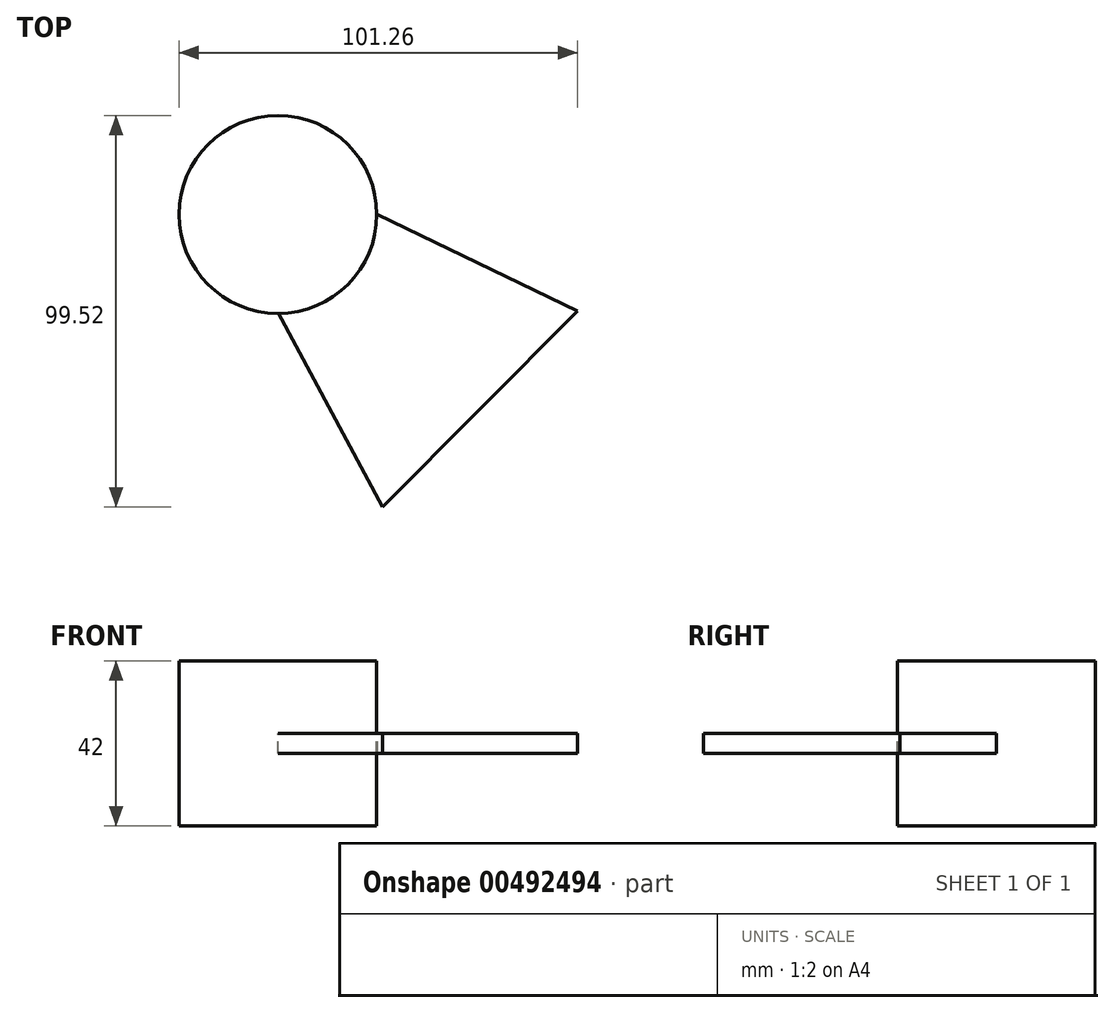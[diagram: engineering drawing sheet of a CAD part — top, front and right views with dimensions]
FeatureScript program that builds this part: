
annotation { "Feature Type Name" : "Feature", "Feature Type Description" : "" }
export const myFeature = defineFeature(function(context is Context, id is Id, definition is map)
    precondition{}
    {
        {
            var Q0;
            Q0=qCreatedBy(makeId("Top.planeOp"),FACE);
            var sketch = newSketch(context, id + "F0", { "sketchPlane" : qUnion([Q0])});
            skCircle(sketch, "E0", {"center": v(0, 0) * mm, "radius": 25.13 * mm});
            skSolve(sketch);
        }
        {
            var Q0;
            Q0=sQuery(id+"F0.wireOp",EDGE,"E0");
            extrude(context, id + "F1", {"bodyType" : ToolBodyType.SURFACE, "surfaceEntities" : qUnion([Q0]), "endBound" : BoundingType.SYMMETRIC, "depth" : 42 * mm});
        }
        {
            var Q0;
            Q0=qCreatedBy(makeId("Top.planeOp"),FACE);
            var sketch = newSketch(context, id + "F2", { "sketchPlane" : qUnion([Q0])});
            skLineSegment(sketch, "E1", {"start": v(25.35, 0) * mm, "end": v(76.13, -24.53) * mm});
            skLineSegment(sketch, "E2", {"start": v(76.13, -24.53) * mm, "end": v(26.56, -74.39) * mm});
            skLineSegment(sketch, "E3", {"start": v(26.56, -74.39) * mm, "end": v(0, -24.95) * mm});
            skSolve(sketch);
        }
        {
            var Q0;
            Q0=sQuery(id+"F2.wireOp",EDGE,"E2");
            var Q1;
            Q1=sQuery(id+"F2.wireOp",EDGE,"E3");
            var Q2;
            Q2=sQuery(id+"F2.wireOp",EDGE,"E1");
            extrude(context, id + "F3", {"bodyType" : ToolBodyType.SURFACE, "surfaceEntities" : qUnion([Q0, Q1, Q2]), "endBound" : BoundingType.SYMMETRIC, "depth" : 5 * mm});
        }
    });
